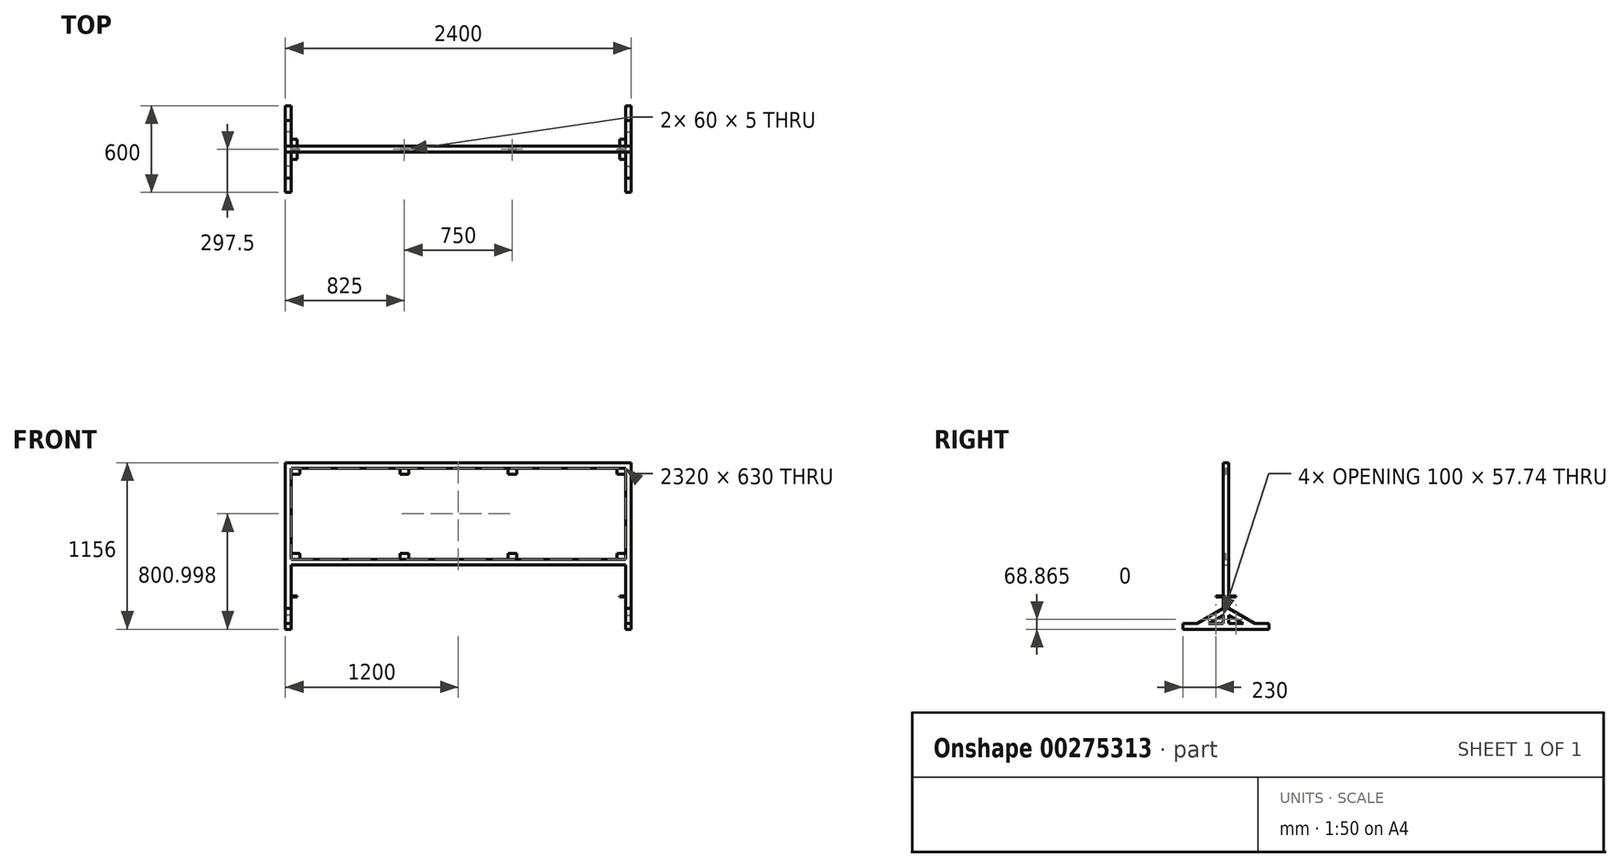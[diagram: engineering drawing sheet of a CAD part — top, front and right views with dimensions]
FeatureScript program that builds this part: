
annotation { "Feature Type Name" : "Feature", "Feature Type Description" : "" }
export const myFeature = defineFeature(function(context is Context, id is Id, definition is map)
    precondition{}
    {
        {
            var Q0;
            Q0=qCreatedBy(makeId("Front.planeOp"),FACE);
            var sketch = newSketch(context, id + "F0", { "sketchPlane" : qUnion([Q0])});
            skLineSegment(sketch, "E0.bottom", {"start": v(-1200, 432.34) * mm, "end": v(1200, 432.34) * mm});
            skLineSegment(sketch, "E0.top", {"start": v(-1200, -277.66) * mm, "end": v(1200, -277.66) * mm});
            skLineSegment(sketch, "E0.left", {"start": v(-1200, 432.34) * mm, "end": v(-1200, -277.66) * mm});
            skLineSegment(sketch, "E0.right", {"start": v(1200, 432.34) * mm, "end": v(1200, -277.66) * mm});
            skLineSegment(sketch, "E1.bottom", {"start": v(-1160, 392.34) * mm, "end": v(1160, 392.34) * mm});
            skLineSegment(sketch, "E1.top", {"start": v(-1160, -237.66) * mm, "end": v(1160, -237.66) * mm});
            skLineSegment(sketch, "E1.left", {"start": v(-1160, 392.34) * mm, "end": v(-1160, -237.66) * mm});
            skLineSegment(sketch, "E1.right", {"start": v(1160, 392.34) * mm, "end": v(1160, -237.66) * mm});
            skLineSegment(sketch, "E2", {"start": v(-1200, -277.66) * mm, "end": v(-1200, -723.66) * mm});
            skLineSegment(sketch, "E3", {"start": v(-1200, -723.66) * mm, "end": v(-1160, -723.66) * mm});
            skLineSegment(sketch, "E4", {"start": v(-1160, -723.66) * mm, "end": v(-1160, -277.66) * mm});
            skLineSegment(sketch, "E5", {"start": v(1200, -277.66) * mm, "end": v(1200, -723.66) * mm});
            skLineSegment(sketch, "E6", {"start": v(1200, -723.66) * mm, "end": v(1160, -723.66) * mm});
            skPoint(sketch, "E6.endSnap0", {"position": v(-1180, -723.66) * mm});
            skLineSegment(sketch, "E7", {"start": v(1160, -723.66) * mm, "end": v(1160, -277.66) * mm});
            skSolve(sketch);
        }
        {
            var Q0;
            Q0=makeQuery(id+"F0.imprint","IMPRINT",FACE,{"disambiguationData":[TD([[makeQuery(id+"F0.imprint","IMPRINT",EDGE,{"derivedFrom":sQuery(id+"F0.wireOp",EDGE,"vreTRAL3-RHGE-12Uy-ID28-2AFktkbIbBq8.bottom")}),1.0]])]});
            var Q1;
            Q1=makeQuery(id+"F0.imprint","IMPRINT",FACE,{"disambiguationData":[TD([[makeQuery(id+"F0.imprint","IMPRINT",EDGE,{"derivedFrom":sQuery(id+"F0.wireOp",EDGE,"mXuv7xjJ-x5BA-lK8Q-WKAj-KdzIBZ5x9POY.bottom")}),1.0]])]});
            var Q2;
            {var subQ1=sQuery(id+"F0.wireOp",EDGE,"E0.left");Q2=makeQuery(id+"F0.imprint","IMPRINT",FACE,{"disambiguationData":[TD([[makeQuery(id+"F0.imprint","IMPRINT",EDGE,{"derivedFrom":subQ1}),1.0]])]});}
            var Q3;
            {var subQ0=sQuery(id+"F0.wireOp",EDGE,"E5");Q3=makeQuery(id+"F0.imprint","IMPRINT",FACE,{"disambiguationData":[TD([[makeQuery(id+"F0.imprint","IMPRINT",EDGE,{"derivedFrom":subQ0}),-1.0]])]});}
            var Q4;
            {var subQ0=sQuery(id+"F0.wireOp",EDGE,"E2");Q4=makeQuery(id+"F0.imprint","IMPRINT",FACE,{"disambiguationData":[TD([[makeQuery(id+"F0.imprint","IMPRINT",EDGE,{"derivedFrom":subQ0}),1.0]])]});}
            extrude(context, id + "F1", {"entities" : qUnion([Q0, Q1, Q2, Q3, Q4]), "depth" : 40 * mm});
        }
        {
            var Q0;
            Q0=makeQuery(id+"F1.opExtrude","SWEPT_FACE",FACE,{"disambiguationData":[OSD([sQuery(id+"F0.wireOp",EDGE,"E0.left"),sQuery(id+"F0.wireOp",EDGE,"E2")])]});
            var sketch = newSketch(context, id + "F2", { "sketchPlane" : qUnion([Q0])});
            skLineSegment(sketch, "E8.bottom", {"start": v(-280, -723.66) * mm, "end": v(320, -723.66) * mm});
            skLineSegment(sketch, "E8.top", {"start": v(-280, -683.66) * mm, "end": v(320, -683.66) * mm});
            skLineSegment(sketch, "E8.left", {"start": v(-280, -723.66) * mm, "end": v(-280, -683.66) * mm});
            skLineSegment(sketch, "E8.right", {"start": v(320, -723.66) * mm, "end": v(320, -683.66) * mm});
            skLineSegment(sketch, "E9", {"start": v(-180, -683.66) * mm, "end": v(0, -579.74) * mm});
            skLineSegment(sketch, "E10", {"start": v(0, -579.74) * mm, "end": v(0, -625.93) * mm});
            skLineSegment(sketch, "E11", {"start": v(0, -625.93) * mm, "end": v(-100, -683.66) * mm});
            skLineSegment(sketch, "E12", {"start": v(40, -579.74) * mm, "end": v(220, -683.66) * mm});
            skLineSegment(sketch, "E13", {"start": v(220, -683.66) * mm, "end": v(140, -683.66) * mm});
            skLineSegment(sketch, "E14", {"start": v(140, -683.66) * mm, "end": v(40, -625.93) * mm});
            skLineSegment(sketch, "E15", {"start": v(40, -625.93) * mm, "end": v(40, -579.74) * mm});
            skSolve(sketch);
        }
        {
            var Q0;
            Q0=makeQuery(id+"F2.imprint","IMPRINT",FACE,{"disambiguationData":[TD([[makeQuery(id+"F2.imprint","IMPRINT",EDGE,{"derivedFrom":sQuery(id+"F2.wireOp",EDGE,"E12")}),-1.0]])]});
            var Q1;
            {var subQ0=sQuery(id+"F2.wireOp",EDGE,"E9");Q1=makeQuery(id+"F2.imprint","IMPRINT",FACE,{"disambiguationData":[TD([[makeQuery(id+"F2.imprint","IMPRINT",EDGE,{"derivedFrom":subQ0}),-1.0]])]});}
            var Q2;
            {var subQ5=sQuery(id+"F2.wireOp",EDGE,"E8.left");Q2=makeQuery(id+"F2.imprint","IMPRINT",FACE,{"disambiguationData":[TD([[makeQuery(id+"F2.imprint","IMPRINT",EDGE,{"derivedFrom":subQ5}),-1.0]])]});}
            var Q3;
            {var subQ6=sQuery(id+"F2.wireOp",EDGE,"E8.right");Q3=makeQuery(id+"F2.imprint","IMPRINT",FACE,{"disambiguationData":[TD([[makeQuery(id+"F2.imprint","IMPRINT",EDGE,{"derivedFrom":subQ6}),1.0]])]});}
            var Q4;
            {var subQ0=sQuery(id+"F2.wireOp",EDGE,"E8.bottom");var subQ1=sQuery(id+"F0.wireOp",EDGE,"E2");var subQ2=sQuery(id+"F0.wireOp",EDGE,"E0.left");var subQ3=makeQuery(id+"F1.opExtrude","CAP_EDGE",EDGE,{"disambiguationData":[OSD([subQ2,subQ1])],"isStart":true});var subQ4=makeQuery(id+"F2.imprint","INTERSECT",VERTEX,{"derivedFrom":[subQ3,subQ0]});var subQ5=makeQuery(id+"F1.opExtrude","CAP_EDGE",EDGE,{"disambiguationData":[OSD([subQ2,subQ1])],"isStart":false});var subQ6=makeQuery(id+"F2.imprint","INTERSECT",VERTEX,{"derivedFrom":[subQ5,subQ0]});Q4=makeQuery(id+"F2.imprint","IMPRINT",FACE,{"disambiguationData":[TD([[makeQuery(id+"F2.imprint","IMPRINT",EDGE,{"disambiguationData":[TD([[subQ4,1.0],[subQ6,-1.0]])],"derivedFrom":subQ0}),-1.0]])]});}
            extrude(context, id + "F3", {"entities" : qUnion([Q0, Q1, Q2, Q3, Q4]), "oppositeDirection" : true, "depth" : 40 * mm});
        }
        {
            var Q0;
            Q0=makeQuery(id+"F3.boolean.opBoolean","MERGE",FACE,{"derivedFrom":[makeQuery(id+"F1.opExtrude","SWEPT_FACE",FACE,{"disambiguationData":[OSD([sQuery(id+"F0.wireOp",EDGE,"E4")])]}),makeQuery(id+"F3.opExtrude","CAP_FACE",FACE,{"disambiguationData":[OSD([sQuery(id+"F2.wireOp",EDGE,"E8.bottom"),sQuery(id+"F2.wireOp",EDGE,"E8.top"),sQuery(id+"F2.wireOp",EDGE,"E8.left"),sQuery(id+"F2.wireOp",EDGE,"E8.right"),sQuery(id+"F2.wireOp",EDGE,"E9"),sQuery(id+"F2.wireOp",EDGE,"E10"),sQuery(id+"F2.wireOp",EDGE,"E11"),sQuery(id+"F2.wireOp",EDGE,"E12"),sQuery(id+"F2.wireOp",EDGE,"E14"),sQuery(id+"F2.wireOp",EDGE,"E15")])],"isStart":false})]});
            var sketch = newSketch(context, id + "F4", { "sketchPlane" : qUnion([Q0])});
            skLineSegment(sketch, "E16.bottom", {"start": v(50, -492.66) * mm, "end": v(-90, -492.66) * mm});
            skLineSegment(sketch, "E16.top", {"start": v(50, -497.66) * mm, "end": v(-90, -497.66) * mm});
            skLineSegment(sketch, "E16.left", {"start": v(-90, -492.66) * mm, "end": v(-90, -497.66) * mm});
            skLineSegment(sketch, "E16.right", {"start": v(50, -492.66) * mm, "end": v(50, -497.66) * mm});
            skPoint(sketch, "E17", {"position": v(-20, -497.66) * mm});
            skSolve(sketch);
        }
        {
            var Q0;
            Q0=makeQuery(id+"F4.imprint","IMPRINT",FACE,{"disambiguationData":[TD([[makeQuery(id+"F4.imprint","IMPRINT",EDGE,{"derivedFrom":sQuery(id+"F4.wireOp",EDGE,"E16.bottom")}),1.0]])]});
            extrude(context, id + "F5", {"entities" : qUnion([Q0]), "depth" : 40 * mm});
        }
        {
            var Q0;
            Q0=makeQuery(id+"F5.opExtrude","SWEPT_BODY",BODY,{"disambiguationData":[OSD([sQuery(id+"F4.wireOp",EDGE,"E16.bottom"),sQuery(id+"F4.wireOp",EDGE,"E16.top"),sQuery(id+"F4.wireOp",EDGE,"E16.left"),sQuery(id+"F4.wireOp",EDGE,"E16.right")])]});
            var Q1;
            Q1=qCreatedBy(makeId("Right.planeOp"),FACE);
            mirror(context, id + "F6", {"operationType" : NewBodyOperationType.ADD, "entities" : qUnion([Q0]), "mirrorPlane" : qUnion([Q1])});
        }
        {
            var Q0;
            Q0=makeQuery(id+"F3.opExtrude","SWEPT_BODY",BODY,{"disambiguationData":[OSD([sQuery(id+"F2.wireOp",EDGE,"E8.bottom"),sQuery(id+"F2.wireOp",EDGE,"E8.top"),sQuery(id+"F2.wireOp",EDGE,"E8.left"),sQuery(id+"F2.wireOp",EDGE,"E8.right"),sQuery(id+"F2.wireOp",EDGE,"E9"),sQuery(id+"F2.wireOp",EDGE,"E10"),sQuery(id+"F2.wireOp",EDGE,"E11"),sQuery(id+"F2.wireOp",EDGE,"E12"),sQuery(id+"F2.wireOp",EDGE,"E14"),sQuery(id+"F2.wireOp",EDGE,"E15")])]});
            var Q1;
            Q1=qCreatedBy(makeId("Right.planeOp"),FACE);
            mirror(context, id + "F7", {"operationType" : NewBodyOperationType.ADD, "entities" : qUnion([Q0]), "mirrorPlane" : qUnion([Q1])});
        }
        {
            var Q0;
            Q0=qCreatedBy(makeId("Front.planeOp"),FACE);
            cPlane(context, id + "F8", {"entities" : qUnion([Q0]), "cplaneType" : CPlaneType.OFFSET, "offset" : 20 * mm, "width" : 150 * mm, "height" : 150 * mm});
        }
        {
            var Q0;
            Q0=qCreatedBy(id+"F8.planeOp",FACE);
            var sketch = newSketch(context, id + "F9", { "sketchPlane" : qUnion([Q0])});
            skLineSegment(sketch, "E18.bottom", {"start": v(-1160, 392.34) * mm, "end": v(-1100, 392.34) * mm});
            skLineSegment(sketch, "E18.top", {"start": v(-1160, 352.34) * mm, "end": v(-1100, 352.34) * mm});
            skLineSegment(sketch, "E18.left", {"start": v(-1160, 392.34) * mm, "end": v(-1160, 352.34) * mm});
            skLineSegment(sketch, "E18.right", {"start": v(-1100, 392.34) * mm, "end": v(-1100, 352.34) * mm});
            skLineSegment(sketch, "E19.bottom", {"start": v(-405, 392.34) * mm, "end": v(-345, 392.34) * mm});
            skLineSegment(sketch, "E19.top", {"start": v(-405, 352.34) * mm, "end": v(-345, 352.34) * mm});
            skLineSegment(sketch, "E19.left", {"start": v(-405, 392.34) * mm, "end": v(-405, 352.34) * mm});
            skLineSegment(sketch, "E19.right", {"start": v(-345, 392.34) * mm, "end": v(-345, 352.34) * mm});
            skLineSegment(sketch, "E20.bottom", {"start": v(345, 392.34) * mm, "end": v(405, 392.34) * mm});
            skLineSegment(sketch, "E20.top", {"start": v(345, 352.34) * mm, "end": v(405, 352.34) * mm});
            skLineSegment(sketch, "E20.left", {"start": v(345, 392.34) * mm, "end": v(345, 352.34) * mm});
            skLineSegment(sketch, "E20.right", {"start": v(405, 392.34) * mm, "end": v(405, 352.34) * mm});
            skLineSegment(sketch, "E21.bottom", {"start": v(1160, 392.34) * mm, "end": v(1100, 392.34) * mm});
            skLineSegment(sketch, "E21.top", {"start": v(1160, 352.34) * mm, "end": v(1100, 352.34) * mm});
            skLineSegment(sketch, "E21.left", {"start": v(1160, 392.34) * mm, "end": v(1160, 352.34) * mm});
            skLineSegment(sketch, "E21.right", {"start": v(1100, 392.34) * mm, "end": v(1100, 352.34) * mm});
            skLineSegment(sketch, "E22.bottom", {"start": v(1160, -237.66) * mm, "end": v(1100, -237.66) * mm});
            skLineSegment(sketch, "E22.top", {"start": v(1160, -197.66) * mm, "end": v(1100, -197.66) * mm});
            skLineSegment(sketch, "E22.left", {"start": v(1160, -237.66) * mm, "end": v(1160, -197.66) * mm});
            skLineSegment(sketch, "E22.right", {"start": v(1100, -237.66) * mm, "end": v(1100, -197.66) * mm});
            skLineSegment(sketch, "E23.bottom", {"start": v(405, -237.66) * mm, "end": v(345, -237.66) * mm});
            skLineSegment(sketch, "E23.top", {"start": v(405, -197.66) * mm, "end": v(345, -197.66) * mm});
            skLineSegment(sketch, "E23.left", {"start": v(405, -237.66) * mm, "end": v(405, -197.66) * mm});
            skLineSegment(sketch, "E23.right", {"start": v(345, -237.66) * mm, "end": v(345, -197.66) * mm});
            skLineSegment(sketch, "E24.bottom", {"start": v(-345, -237.66) * mm, "end": v(-405, -237.66) * mm});
            skLineSegment(sketch, "E24.top", {"start": v(-345, -197.66) * mm, "end": v(-405, -197.66) * mm});
            skLineSegment(sketch, "E24.left", {"start": v(-345, -237.66) * mm, "end": v(-345, -197.66) * mm});
            skLineSegment(sketch, "E24.right", {"start": v(-405, -237.66) * mm, "end": v(-405, -197.66) * mm});
            skLineSegment(sketch, "E25.bottom", {"start": v(-1100, -237.66) * mm, "end": v(-1160, -237.66) * mm});
            skLineSegment(sketch, "E25.top", {"start": v(-1100, -197.66) * mm, "end": v(-1160, -197.66) * mm});
            skLineSegment(sketch, "E25.left", {"start": v(-1100, -237.66) * mm, "end": v(-1100, -197.66) * mm});
            skLineSegment(sketch, "E25.right", {"start": v(-1160, -237.66) * mm, "end": v(-1160, -197.66) * mm});
            skSolve(sketch);
        }
        {
            var Q0;
            Q0=makeQuery(id+"F9.imprint","IMPRINT",FACE,{"disambiguationData":[TD([[makeQuery(id+"F9.imprint","IMPRINT",EDGE,{"derivedFrom":sQuery(id+"F9.wireOp",EDGE,"E25.bottom")}),-1.0]])]});
            var Q1;
            Q1=makeQuery(id+"F9.imprint","IMPRINT",FACE,{"disambiguationData":[TD([[makeQuery(id+"F9.imprint","IMPRINT",EDGE,{"derivedFrom":sQuery(id+"F9.wireOp",EDGE,"E18.bottom")}),-1.0]])]});
            var Q2;
            Q2=makeQuery(id+"F9.imprint","IMPRINT",FACE,{"disambiguationData":[TD([[makeQuery(id+"F9.imprint","IMPRINT",EDGE,{"derivedFrom":sQuery(id+"F9.wireOp",EDGE,"E19.bottom")}),-1.0]])]});
            var Q3;
            Q3=makeQuery(id+"F9.imprint","IMPRINT",FACE,{"disambiguationData":[TD([[makeQuery(id+"F9.imprint","IMPRINT",EDGE,{"derivedFrom":sQuery(id+"F9.wireOp",EDGE,"E24.bottom")}),-1.0]])]});
            var Q4;
            Q4=makeQuery(id+"F9.imprint","IMPRINT",FACE,{"disambiguationData":[TD([[makeQuery(id+"F9.imprint","IMPRINT",EDGE,{"derivedFrom":sQuery(id+"F9.wireOp",EDGE,"E23.bottom")}),-1.0]])]});
            var Q5;
            Q5=makeQuery(id+"F9.imprint","IMPRINT",FACE,{"disambiguationData":[TD([[makeQuery(id+"F9.imprint","IMPRINT",EDGE,{"derivedFrom":sQuery(id+"F9.wireOp",EDGE,"E20.bottom")}),-1.0]])]});
            var Q6;
            Q6=makeQuery(id+"F9.imprint","IMPRINT",FACE,{"disambiguationData":[TD([[makeQuery(id+"F9.imprint","IMPRINT",EDGE,{"derivedFrom":sQuery(id+"F9.wireOp",EDGE,"E21.bottom")}),1.0]])]});
            var Q7;
            Q7=makeQuery(id+"F9.imprint","IMPRINT",FACE,{"disambiguationData":[TD([[makeQuery(id+"F9.imprint","IMPRINT",EDGE,{"derivedFrom":sQuery(id+"F9.wireOp",EDGE,"E22.bottom")}),-1.0]])]});
            extrude(context, id + "F10", {"entities" : qUnion([Q0, Q1, Q2, Q3, Q4, Q5, Q6, Q7]), "operationType" : NewBodyOperationType.ADD, "depth" : 5 * mm});
        }
    });
